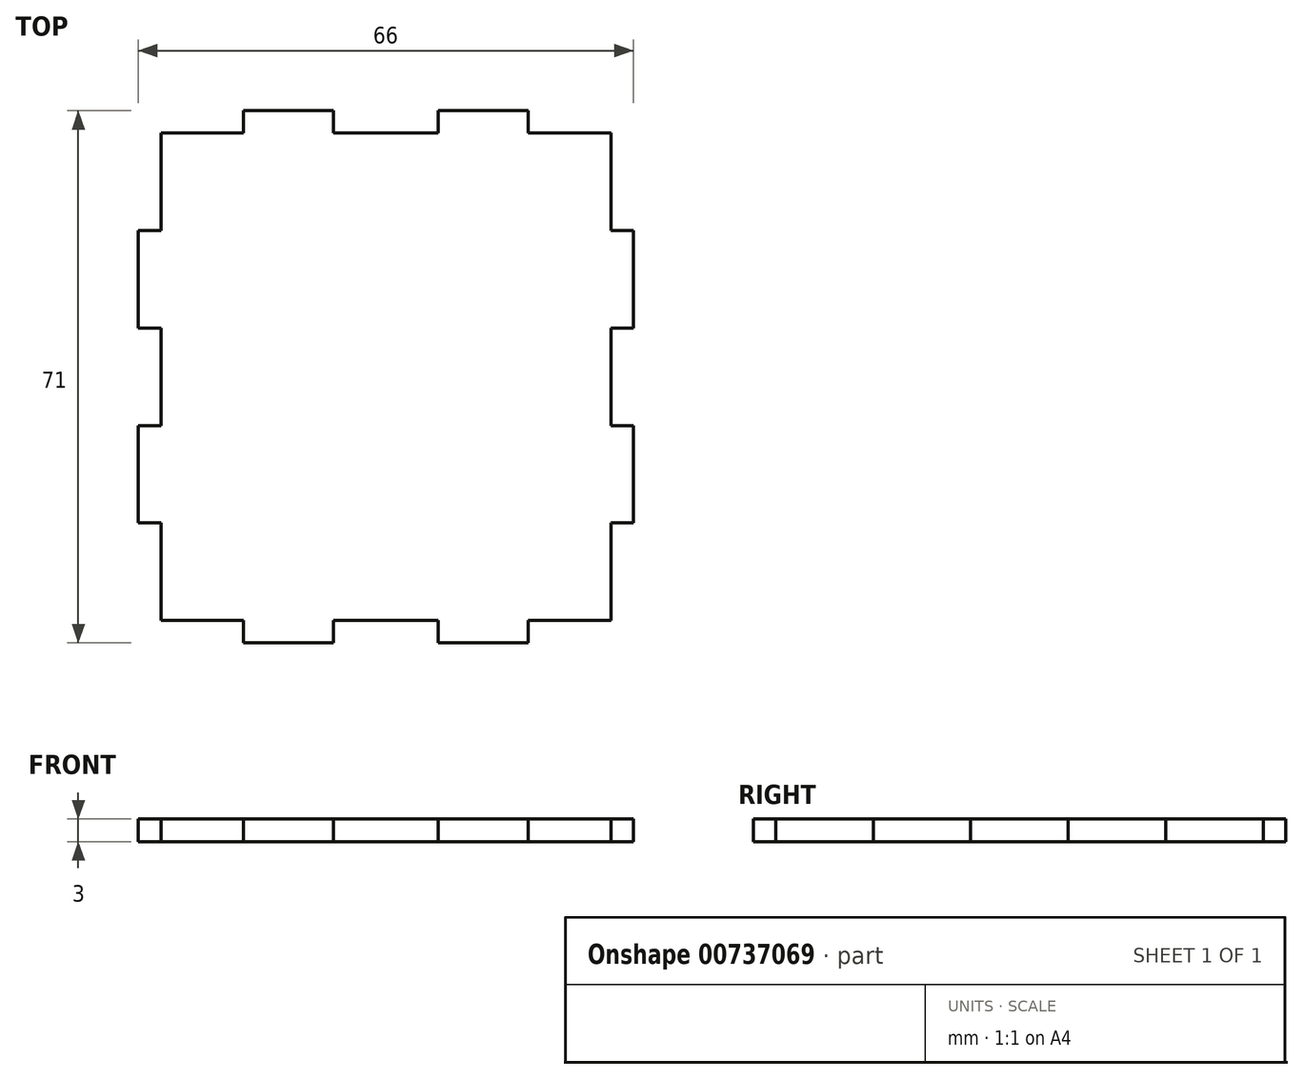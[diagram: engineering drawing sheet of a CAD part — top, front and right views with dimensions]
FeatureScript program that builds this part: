
annotation { "Feature Type Name" : "Feature", "Feature Type Description" : "" }
export const myFeature = defineFeature(function(context is Context, id is Id, definition is map)
    precondition{}
    {
        {
            var Q0;
            Q0=qCreatedBy(makeId("Top.planeOp"),FACE);
            var sketch = newSketch(context, id + "F0", { "sketchPlane" : qUnion([Q0])});
            skLineSegment(sketch, "E0", {"start": v(-33, 35.5) * mm, "end": v(-33, -35.5) * mm, "construction": true});
            skLineSegment(sketch, "E1", {"start": v(-33, -35.5) * mm, "end": v(33, -35.5) * mm, "construction": true});
            skLineSegment(sketch, "E2", {"start": v(33, -35.5) * mm, "end": v(33, 35.5) * mm, "construction": true});
            skLineSegment(sketch, "E3", {"start": v(33, 35.5) * mm, "end": v(-33, 35.5) * mm, "construction": true});
            skLineSegment(sketch, "E4", {"start": v(-33, -32.5) * mm, "end": v(-19, -32.5) * mm});
            skLineSegment(sketch, "E5", {"start": v(-19, -32.5) * mm, "end": v(-19, -35.5) * mm});
            skLineSegment(sketch, "E6", {"start": v(-19, -35.5) * mm, "end": v(-7, -35.5) * mm});
            skLineSegment(sketch, "E7", {"start": v(-7, -35.5) * mm, "end": v(-7, -32.5) * mm});
            skLineSegment(sketch, "E8", {"start": v(-7, -32.5) * mm, "end": v(7, -32.5) * mm});
            skLineSegment(sketch, "E9", {"start": v(7, -32.5) * mm, "end": v(7, -35.5) * mm});
            skLineSegment(sketch, "E10", {"start": v(7, -35.5) * mm, "end": v(19, -35.5) * mm});
            skLineSegment(sketch, "E11", {"start": v(19, -35.5) * mm, "end": v(19, -32.5) * mm});
            skLineSegment(sketch, "E12", {"start": v(19, -32.5) * mm, "end": v(33, -32.5) * mm});
            skLineSegment(sketch, "E13", {"start": v(30, -32.5) * mm, "end": v(30, -19.5) * mm});
            skLineSegment(sketch, "E14", {"start": v(30, -19.5) * mm, "end": v(33, -19.5) * mm});
            skLineSegment(sketch, "E15", {"start": v(33, -19.5) * mm, "end": v(33, -6.5) * mm});
            skLineSegment(sketch, "E16", {"start": v(33, -6.5) * mm, "end": v(30, -6.5) * mm});
            skLineSegment(sketch, "E17", {"start": v(30, -6.5) * mm, "end": v(30, 6.5) * mm});
            skLineSegment(sketch, "E18", {"start": v(30, 6.5) * mm, "end": v(33, 6.5) * mm});
            skLineSegment(sketch, "E19", {"start": v(33, 6.5) * mm, "end": v(33, 19.5) * mm});
            skLineSegment(sketch, "E20", {"start": v(33, 19.5) * mm, "end": v(30, 19.5) * mm});
            skLineSegment(sketch, "E21", {"start": v(30, 19.5) * mm, "end": v(30, 32.5) * mm});
            skLineSegment(sketch, "E22", {"start": v(30, 32.5) * mm, "end": v(33, 32.5) * mm});
            skLineSegment(sketch, "E23", {"start": v(33, 32.5) * mm, "end": v(33, 32.5) * mm});
            skLineSegment(sketch, "E24", {"start": v(-33, 32.5) * mm, "end": v(-19, 32.5) * mm});
            skLineSegment(sketch, "E25", {"start": v(-19, 32.5) * mm, "end": v(-19, 35.5) * mm});
            skLineSegment(sketch, "E26", {"start": v(-19, 35.5) * mm, "end": v(-7, 35.5) * mm});
            skLineSegment(sketch, "E27", {"start": v(-7, 35.5) * mm, "end": v(-7, 32.5) * mm});
            skLineSegment(sketch, "E28", {"start": v(-7, 32.5) * mm, "end": v(7, 32.5) * mm});
            skLineSegment(sketch, "E29", {"start": v(7, 32.5) * mm, "end": v(7, 35.5) * mm});
            skLineSegment(sketch, "E30", {"start": v(7, 35.5) * mm, "end": v(19, 35.5) * mm});
            skLineSegment(sketch, "E31", {"start": v(19, 35.5) * mm, "end": v(19, 32.5) * mm});
            skLineSegment(sketch, "E32", {"start": v(19, 32.5) * mm, "end": v(33, 32.5) * mm});
            skLineSegment(sketch, "E33", {"start": v(-30, -32.5) * mm, "end": v(-30, -19.5) * mm});
            skPoint(sketch, "E33.endSnap0", {"position": v(31.5, -19.5) * mm});
            skLineSegment(sketch, "E34", {"start": v(-30, -19.5) * mm, "end": v(-33, -19.5) * mm});
            skLineSegment(sketch, "E35", {"start": v(-33, -19.5) * mm, "end": v(-33, -6.5) * mm});
            skLineSegment(sketch, "E36", {"start": v(-33, -6.5) * mm, "end": v(-30, -6.5) * mm});
            skLineSegment(sketch, "E37", {"start": v(-30, -6.5) * mm, "end": v(-30, 6.5) * mm});
            skLineSegment(sketch, "E38", {"start": v(-30, 6.5) * mm, "end": v(-33, 6.5) * mm});
            skLineSegment(sketch, "E39", {"start": v(-33, 6.5) * mm, "end": v(-33, 19.5) * mm});
            skLineSegment(sketch, "E40", {"start": v(-33, 19.5) * mm, "end": v(-30, 19.5) * mm});
            skLineSegment(sketch, "E41", {"start": v(-30, 19.5) * mm, "end": v(-30, 32.5) * mm});
            skSolve(sketch);
        }
        {
            var Q0;
            {var subQ4=sQuery(id+"F0.wireOp",EDGE,"E5");Q0=makeQuery(id+"F0.imprint","IMPRINT",FACE,{"disambiguationData":[TD([[makeQuery(id+"F0.imprint","IMPRINT",EDGE,{"derivedFrom":subQ4}),1.0]])]});}
            extrude(context, id + "F1", {"entities" : qUnion([Q0]), "depth" : 3 * mm, "offsetDistance" : 25 * mm});
        }
    });
